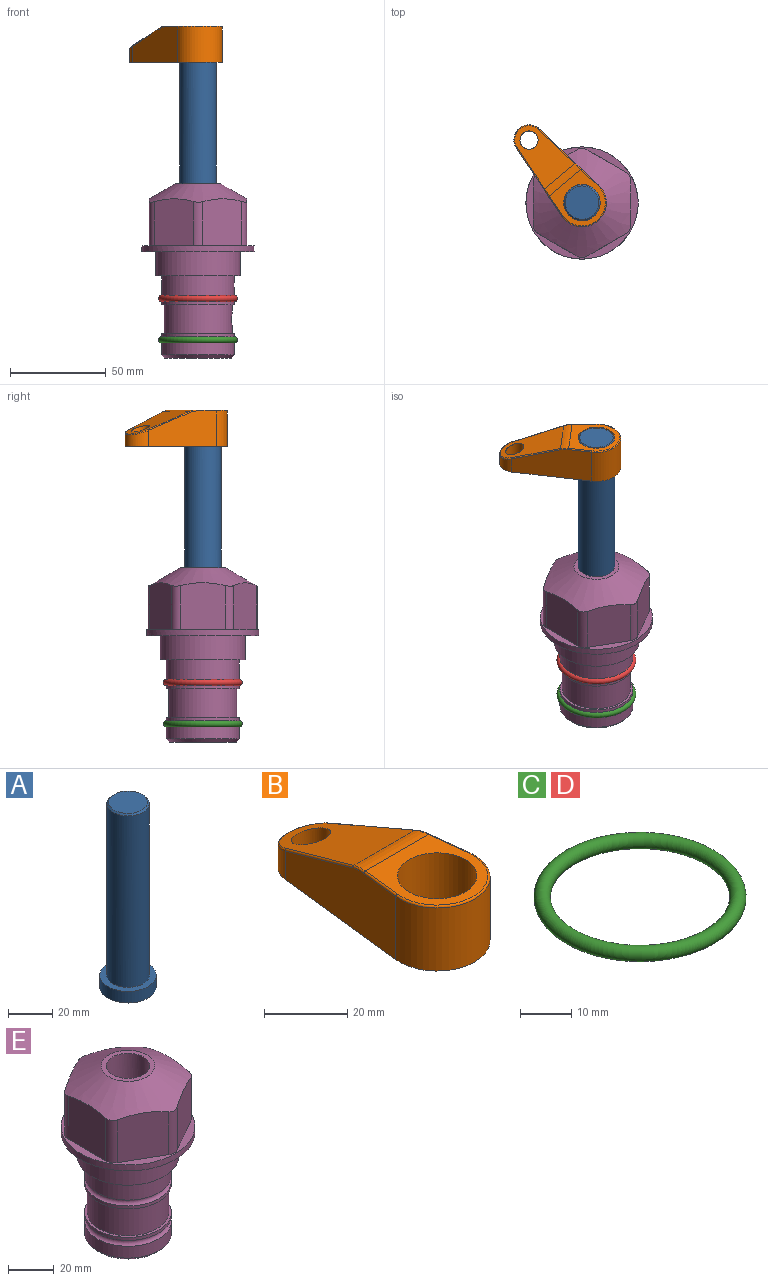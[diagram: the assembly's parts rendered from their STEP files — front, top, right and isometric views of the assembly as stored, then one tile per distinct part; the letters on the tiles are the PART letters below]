
ASSEMBLY  parts=5 mates=3
PART A: 6 faces, bbox 25.4x25.4x101.6 mm
  f0: plane 17.46x17.46mm, normal (0,0,1), area 239.5mm2, adj f5
  f1: plane 25.4x25.4mm, normal (0,0,-1), area 506.7mm2, adj f2
  f2: cylinder r=12.7mm len=25.4mm, axis (0,0,1), area 506.7mm2, adj f1,f3
  f3: plane 25.4x25.4mm, normal (0,0,1), area 221.7mm2, adj f2,f4
  f4: cylinder r=9.53mm len=94.46mm, axis (0,0,1), area 5653mm2, adj f3,f5
  f5: cone r=8.73mm half-angle=45deg, axis (0,0,-1), area 64.4mm2, adj f0,f4
PART B: 44 faces, bbox 27.5x64.5x19.1 mm
  f0: plane 2.3x0.95mm, normal (0,0,-1), area 1mm2, adj f25,f30,f34
  f1: plane 63.5x25.4mm, normal (0,0,-1), area 561.7mm2, adj f2,f3,f4,f5,f6,f7,f19,f20
  f2: cylinder r=12.7mm len=25.4mm, axis (0,0,-1), area 792.2mm2, adj f1,f3,f5,f13
  f3: plane 42.33x18.54mm, normal (0.99,0.11,0), area 647mm2, adj f1,f2,f4,f11,f12,f14
  f4: cylinder r=7.94mm len=15.78mm, axis (0,0,-1), area 158.6mm2, adj f1,f3,f5,f16
  f5: plane 42.33x18.54mm, normal (-0.99,0.11,0), area 647mm2, adj f1,f2,f4,f15,f17,f18
  f6: cylinder r=9.53mm len=19.05mm, axis (0,0,-1), area 1140.1mm2, adj f1,f8
  f7: cylinder r=4.76mm len=10.98mm, axis (0,0,-1), area 276.1mm2, adj f1,f9
  f8: plane 25.83x24.38mm, normal (0,0,1), area 262.2mm2, adj f6,f10,f11,f13,f15
  f9: plane 32.49x20.55mm, normal (0,0.34,0.94), area 489.9mm2, adj f7,f10,f14,f16,f18
  f10: cylinder r=12.7mm len=21.49mm, axis (-1,0,0), area 93.2mm2, adj f8,f9,f12,f17
  f11: cylinder r=0.51mm len=12.34mm, axis (0.11,-0.99,0), area 9.9mm2, adj f3,f8,f12,f13
  f12: bspline ~7.62x1.64mm, area 3.5mm2, adj f3,f10,f11,f14
  f13: torus R=12.19mm, axis (0,0,1), area 33.6mm2, adj f2,f8,f11,f15
  f14: cylinder r=0.51mm len=26.01mm, axis (0.1,-0.93,0.34), area 21.6mm2, adj f3,f9,f12,f16
  f15: cylinder r=0.51mm len=12.34mm, axis (0.11,0.99,0), area 9.9mm2, adj f5,f8,f13,f17
  f16: bspline ~15.78x7.05mm, area 15.7mm2, adj f4,f9,f14,f18
  f17: bspline ~7.62x1.64mm, area 3.5mm2, adj f5,f10,f15,f18
  f18: cylinder r=0.51mm len=26.01mm, axis (0.1,0.93,-0.34), area 21.6mm2, adj f5,f9,f16,f17
  f19: plane 21.6x14.29mm, normal (-0.99,-0.11,0), area 242.6mm2, adj f1,f26,f28,f34,f36,f38
  f20: plane 21.6x14.29mm, normal (0.99,-0.11,0), area 242.6mm2, adj f1,f27,f29,f37,f39,f41
  f21: cylinder r=12.7mm len=14.29mm, axis (0,0,-1), area 173.2mm2, adj f1,f26,f27,f30,f31,f33
  f22: cylinder r=7.94mm len=7.63mm, axis (0,0,-1), area 53.8mm2, adj f1,f28,f29,f42
  f23: plane 2.3x0.95mm, normal (0,0,-1), area 1mm2, adj f25,f33,f37
  f24: plane 17.94x12.32mm, normal (0,-0.34,-0.94), area 191.2mm2, adj f25,f38,f41,f42
  f25: cylinder r=9.53mm len=12.93mm, axis (-1,0,0), area 37.5mm2, adj f0,f23,f24,f31,f36,f39
  f26: cylinder r=1.59mm len=14.29mm, axis (0,0,-1), area 49mm2, adj f1,f19,f21,f32
  f27: cylinder r=1.59mm len=14.29mm, axis (0,0,-1), area 49mm2, adj f1,f20,f21,f35
  f28: cylinder r=1.59mm len=7.28mm, axis (0,0,-1), area 22.1mm2, adj f1,f19,f22,f40
  f29: cylinder r=1.59mm len=7.28mm, axis (0,0,-1), area 22.1mm2, adj f1,f20,f22,f43
  f30: torus R=14.29mm, axis (0,0,1), area 5.8mm2, adj f0,f21,f31,f32
  f31: bspline ~11.06x2.73mm, area 20.8mm2, adj f21,f25,f30,f33
  f32: sphere r=1.59mm, area 5.4mm2, adj f26,f30,f34
  f33: torus R=14.29mm, axis (0,0,1), area 5.8mm2, adj f21,f23,f31,f35
  f34: cylinder r=1.59mm len=1.68mm, axis (-0.11,0.99,0), area 2.4mm2, adj f0,f19,f32,f36
  f35: sphere r=1.59mm, area 5.4mm2, adj f27,f33,f37
  f36: bspline ~5.82x2.33mm, area 7.7mm2, adj f19,f25,f34,f38
  f37: cylinder r=1.59mm len=1.68mm, axis (0.11,0.99,0), area 2.4mm2, adj f20,f23,f35,f39
  f38: cylinder r=1.59mm len=18.33mm, axis (0.1,-0.93,0.34), area 46.7mm2, adj f19,f24,f36,f40
  f39: bspline ~5.82x2.33mm, area 7.7mm2, adj f20,f25,f37,f41
  f40: sphere r=1.59mm, area 3.6mm2, adj f28,f38,f42
  f41: cylinder r=1.59mm len=18.33mm, axis (0.1,0.93,-0.34), area 46.7mm2, adj f20,f24,f39,f43
  f42: bspline ~8.31x1.84mm, area 15.3mm2, adj f22,f24,f40,f43
  f43: sphere r=1.59mm, area 3.6mm2, adj f29,f41,f42
PART C: 1 faces, bbox 44.7x44.7x3.2 mm
  f0: torus R=19.05mm, axis (0,0,1), area 1193.9mm2
PART D: same geometry as C
PART E: 36 faces, bbox 58.7x58.7x91.2 mm
  f0: cylinder r=17.78mm len=35.56mm, axis (0,0,1), area 1670.8mm2, adj f23,f24,f31
  f1: cylinder r=19.05mm len=38.1mm, axis (0,0,1), area 1191.9mm2, adj f26,f27,f30
  f2: plane 58.66x58.66mm, normal (0,0,-1), area 1150.6mm2, adj f3,f28
  f3: cylinder r=29.33mm len=58.66mm, axis (0,0,-1), area 585.1mm2, adj f2,f4
  f4: plane 58.66x58.66mm, normal (0,0,1), area 475.9mm2, adj f3,f5,f6,f7,f8,f9,f10,f11
  f5: plane 24.5x20.32mm, normal (-0.5,0.87,0), area 562.8mm2, adj f4,f15,f16,f17
  f6: plane 24.5x20.32mm, normal (0.5,0.87,0), area 562.8mm2, adj f4,f14,f15,f17
  f7: plane 24.5x23.48mm, normal (1,0,0), area 562.8mm2, adj f4,f13,f14,f17
  f8: plane 24.5x20.32mm, normal (0.5,-0.87,0), area 562.8mm2, adj f4,f12,f13,f17
  f9: plane 24.5x20.32mm, normal (-0.5,-0.87,0), area 562.8mm2, adj f4,f11,f12,f17
  f10: plane 24.5x23.48mm, normal (-1,0,0), area 562.8mm2, adj f4,f11,f16,f17
  f11: cylinder r=5.08mm len=23.01mm, axis (0,0,-1), area 121.2mm2, adj f4,f9,f10,f17
  f12: cylinder r=5.08mm len=23.01mm, axis (0,0,-1), area 121.2mm2, adj f4,f8,f9,f17
  f13: cylinder r=5.08mm len=23.01mm, axis (0,0,-1), area 121.2mm2, adj f4,f7,f8,f17
  f14: cylinder r=5.08mm len=23.01mm, axis (0,0,-1), area 121.2mm2, adj f4,f6,f7,f17
  f15: cylinder r=5.08mm len=23.01mm, axis (0,0,-1), area 121.2mm2, adj f4,f5,f6,f17
  f16: cylinder r=5.08mm len=23.01mm, axis (0,0,-1), area 121.2mm2, adj f4,f5,f10,f17
  f17: cone r=11.73mm half-angle=60deg, axis (0,0,-1), area 2071.8mm2, adj f5,f6,f7,f8,f9,f10,f11,f12
  f18: plane 23.46x23.46mm, normal (0,0,1), area 147.4mm2, adj f17,f35
  f19: plane 34.93x34.93mm, normal (0,0,-1), area 958mm2, adj f29
  f20: cylinder r=19.05mm len=38.1mm, axis (0,0,1), area 760.1mm2, adj f21,f29
  f21: torus R=19.05mm, axis (0,0,1), area 565.3mm2, adj f20,f22
  f22: cylinder r=19.05mm len=38.1mm, axis (0,0,1), area 190mm2, adj f21,f23
  f23: plane 38.1x38.1mm, normal (0,0,1), area 146.9mm2, adj f0,f22
  f24: plane 38.1x38.1mm, normal (0,0,-1), area 146.9mm2, adj f0,f25
  f25: cylinder r=19.05mm len=38.1mm, axis (0,0,1), area 190mm2, adj f24,f26
  f26: torus R=19.05mm, axis (0,0,1), area 565.3mm2, adj f1,f25
  f27: plane 44.45x44.45mm, normal (0,0,-1), area 411.7mm2, adj f1,f28
  f28: cylinder r=22.23mm len=44.45mm, axis (0,0,1), area 1773.5mm2, adj f2,f27
  f29: cone r=19.05mm half-angle=45deg, axis (0,0,1), area 257.5mm2, adj f19,f20
  f30: cylinder r=3.17mm len=6.75mm, axis (-1,0,0), area 128mm2, adj f1,f33
  f31: cylinder r=3.17mm len=6.35mm, axis (-1,0,0), area 102.5mm2, adj f0,f33
  f32: plane 25.4x25.4mm, normal (0,0,1), area 506.7mm2, adj f33
  f33: cylinder r=12.7mm len=66.42mm, axis (0,0,-1), area 5236.2mm2, adj f30,f31,f32,f34
  f34: cone r=9.53mm half-angle=30deg, axis (0,0,-1), area 443.4mm2, adj f33,f35
  f35: cylinder r=9.53mm len=19.05mm, axis (0,0,-1), area 849mm2, adj f18,f34
PLACE A rot(axis=(0,0,1),130.2deg) t=(0,0,44.33)mm
PLACE B rot(axis=(0,0,1),40.2deg) t=(0,0,98.94)mm
PLACE C t=(0,0,-21.59)mm
PLACE D at identity
PLACE E at identity fixed
MATE fastened C.f0 <-> E.f0  axis (0,0,1) through (0,0,-46.1)mm
MATE cylindrical A.f2 <-> E.f0  axis (0,0,1) through (0,0,69.96)mm
MATE fastened B.f2 <-> A.f2  axis (0,0,1) through (0,0,117.99)mm
